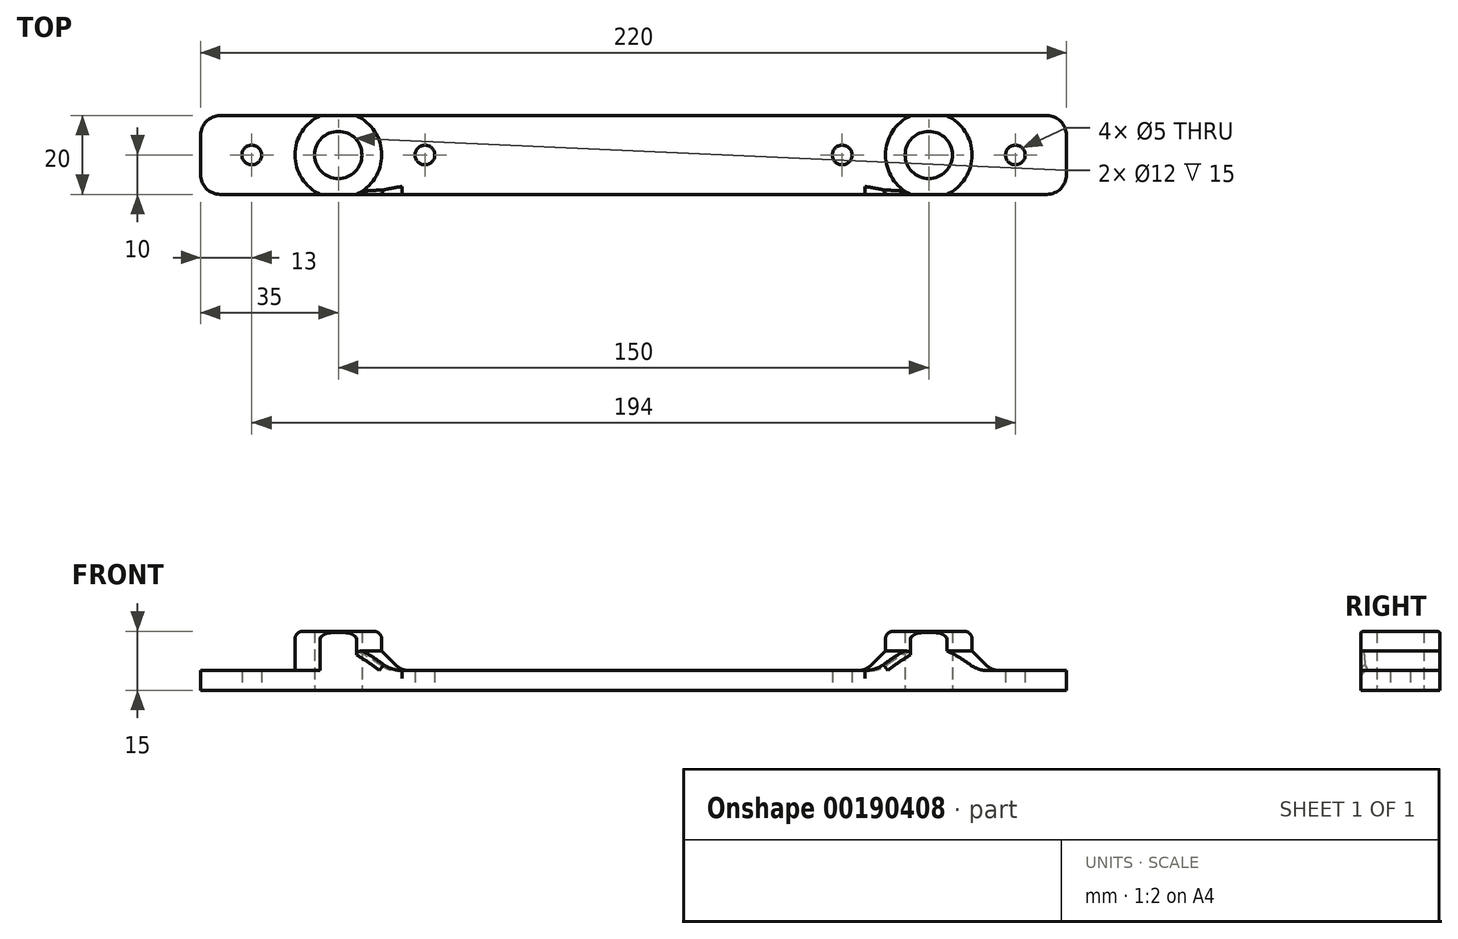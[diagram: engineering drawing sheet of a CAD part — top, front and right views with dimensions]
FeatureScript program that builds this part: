
annotation { "Feature Type Name" : "Feature", "Feature Type Description" : "" }
export const myFeature = defineFeature(function(context is Context, id is Id, definition is map)
    precondition{}
    {
        {
            var Q0;
            Q0=qCreatedBy(makeId("Top.planeOp"),FACE);
            var sketch = newSketch(context, id + "F0", { "sketchPlane" : qUnion([Q0])});
            skLineSegment(sketch, "E0.bottom", {"start": v(105, -10) * mm, "end": v(-105, -10) * mm});
            skLineSegment(sketch, "E0.top", {"start": v(105, 10) * mm, "end": v(-105, 10) * mm});
            skLineSegment(sketch, "E0.left", {"start": v(110, -5) * mm, "end": v(110, 5) * mm});
            skLineSegment(sketch, "E0.right", {"start": v(-110, -5) * mm, "end": v(-110, 5) * mm});
            skPoint(sketch, "E0.middle", {"position": v(0, 0) * mm});
            skCircle(sketch, "E1", {"center": v(-75, 0) * mm, "radius": 6 * mm});
            skCircle(sketch, "E2", {"center": v(75, 0) * mm, "radius": 6 * mm});
            skCircle(sketch, "E3", {"center": v(-53, 0) * mm, "radius": 2.5 * mm});
            skLineSegment(sketch, "E4", {"start": v(-75, 0) * mm, "end": v(-75, 26.01) * mm, "construction": true});
            skCircle(sketch, "E5.MirrorC", {"center": v(-97, 0) * mm, "radius": 2.5 * mm});
            skCircle(sketch, "E6.MirrorC", {"center": v(97, 0) * mm, "radius": 2.5 * mm});
            skCircle(sketch, "E7.MirrorC", {"center": v(53, 0) * mm, "radius": 2.5 * mm});
            skPoint(sketch, "E8.visualSharp", {"position": v(-110, 10) * mm});
            skArc(sketch, "E8.filletArc", {"start": v(-105, 10) * mm, "mid": v(-108.54, 8.54) * mm, "end": v(-110, 5) * mm});
            skPoint(sketch, "E9.visualSharp", {"position": v(-110, -10) * mm});
            skArc(sketch, "E9.filletArc", {"start": v(-110, -5) * mm, "mid": v(-108.54, -8.54) * mm, "end": v(-105, -10) * mm});
            skPoint(sketch, "E10.visualSharp", {"position": v(110, 10) * mm});
            skArc(sketch, "E10.filletArc", {"start": v(110, 5) * mm, "mid": v(108.54, 8.54) * mm, "end": v(105, 10) * mm});
            skPoint(sketch, "E11.visualSharp", {"position": v(110, -10) * mm});
            skArc(sketch, "E11.filletArc", {"start": v(105, -10) * mm, "mid": v(108.54, -8.54) * mm, "end": v(110, -5) * mm});
            skSolve(sketch);
        }
        {
            var Q0;
            Q0 = qSketchRegion(id + "F0", true);
            extrude(context, id + "F1", {"entities" : qUnion([Q0]), "depth" : 5 * mm});
        }
        {
            var Q0;
            Q0=makeQuery(id+"F1.opExtrude","CAP_FACE",FACE,{"disambiguationData":[OSD([sQuery(id+"F0.wireOp",EDGE,"E0.bottom"),sQuery(id+"F0.wireOp",EDGE,"E0.top"),sQuery(id+"F0.wireOp",EDGE,"E0.left"),sQuery(id+"F0.wireOp",EDGE,"E0.right"),sQuery(id+"F0.wireOp",EDGE,"E1"),sQuery(id+"F0.wireOp",EDGE,"E2"),sQuery(id+"F0.wireOp",EDGE,"E3"),sQuery(id+"F0.wireOp",EDGE,"E5.MirrorC"),sQuery(id+"F0.wireOp",EDGE,"E6.MirrorC"),sQuery(id+"F0.wireOp",EDGE,"E7.MirrorC")])],"isStart":false});
            var sketch = newSketch(context, id + "F2", { "sketchPlane" : qUnion([Q0])});
            skArc(sketch, "E12", {"start": v(-79.58, 10) * mm, "mid": v(-86, 0) * mm, "end": v(-79.58, -10) * mm});
            skLineSegment(sketch, "E13.0", {"start": v(-70.42, 10) * mm, "end": v(-79.58, 10) * mm});
            skLineSegment(sketch, "E14.0", {"start": v(-70.42, -10) * mm, "end": v(-79.58, -10) * mm});
            skPoint(sketch, "E15.orphan", {"position": v(105, 10) * mm});
            skPoint(sketch, "E16.orphan", {"position": v(105, -10) * mm});
            skArc(sketch, "E17.trimOffspring", {"start": v(-70.42, -10) * mm, "mid": v(-64, 0) * mm, "end": v(-70.42, 10) * mm});
            skArc(sketch, "E18.MirrorCS", {"start": v(70.42, -10) * mm, "mid": v(64, 0) * mm, "end": v(70.42, 10) * mm});
            skLineSegment(sketch, "E19.MirrorCS", {"start": v(70.42, -10) * mm, "end": v(79.58, -10) * mm});
            skLineSegment(sketch, "E20.MirrorCS", {"start": v(70.42, 10) * mm, "end": v(79.58, 10) * mm});
            skArc(sketch, "E21.MirrorCS", {"start": v(79.58, 10) * mm, "mid": v(86, 0) * mm, "end": v(79.58, -10) * mm});
            skCircle(sketch, "E22.0", {"center": v(-75, 0) * mm, "radius": 6 * mm});
            skCircle(sketch, "E23.0", {"center": v(75, 0) * mm, "radius": 6 * mm});
            skSolve(sketch);
        }
        {
            var Q0;
            Q0 = qSketchRegion(id + "F2", true);
            extrude(context, id + "F3", {"entities" : qUnion([Q0]), "operationType" : NewBodyOperationType.ADD, "depth" : 10 * mm});
        }
        {
            var Q0;
            Q0=makeQuery(id+"F3.opExtrude","CAP_EDGE",EDGE,{"disambiguationData":[OSD([sQuery(id+"F2.wireOp",EDGE,"E12")])],"isStart":true});
            var Q1;
            Q1=makeQuery(id+"F3.opExtrude","CAP_EDGE",EDGE,{"disambiguationData":[OSD([sQuery(id+"F2.wireOp",EDGE,"E17.trimOffspring")])],"isStart":true});
            var Q2;
            Q2=makeQuery(id+"F3.opExtrude","CAP_EDGE",EDGE,{"disambiguationData":[OSD([sQuery(id+"F2.wireOp",EDGE,"E18.MirrorCS")])],"isStart":true});
            var Q3;
            Q3=makeQuery(id+"F3.opExtrude","CAP_EDGE",EDGE,{"disambiguationData":[OSD([sQuery(id+"F2.wireOp",EDGE,"E21.MirrorCS")])],"isStart":true});
            chamfer(context, id + "F4", {"entities" : qUnion([Q0, Q1, Q2, Q3]), "width" : 5 * mm, "tangentPropagation" : true});
        }
        {
            var Q0;
            {var subQ0=sQuery(id+"F0.wireOp",EDGE,"E9.filletArc");var subQ1=sQuery(id+"F0.wireOp",EDGE,"E0.bottom");var subQ2=sQuery(id+"F2.wireOp",EDGE,"E12");var subQ3=sQuery(id+"F0.wireOp",EDGE,"E0.top");var subQ4=sQuery(id+"F0.wireOp",EDGE,"E5.MirrorC");var subQ5=sQuery(id+"F0.wireOp",EDGE,"E8.filletArc");var subQ6=sQuery(id+"F0.wireOp",EDGE,"E0.right");Q0=makeQuery(id+"F4.opChamfer","BLEND_EDGE",EDGE,{"blendedFrom":[makeQuery(id+"F3.opExtrude","CAP_EDGE",EDGE,{"disambiguationData":[OSD([subQ2])],"isStart":true}),makeQuery(id+"F3.boolean.opBoolean","SPLIT",FACE,{"disambiguationData":[TD([makeQuery(id+"F1.opExtrude","SWEPT_FACE",FACE,{"disambiguationData":[OSD([subQ6])]})])],"derivedFrom":makeQuery(id+"F1.opExtrude","CAP_FACE",FACE,{"disambiguationData":[OSD([subQ1,subQ3,sQuery(id+"F0.wireOp",EDGE,"E0.left"),subQ6,sQuery(id+"F0.wireOp",EDGE,"E1"),sQuery(id+"F0.wireOp",EDGE,"E2"),sQuery(id+"F0.wireOp",EDGE,"E3"),subQ4,sQuery(id+"F0.wireOp",EDGE,"E6.MirrorC"),sQuery(id+"F0.wireOp",EDGE,"E7.MirrorC"),subQ5,subQ0,sQuery(id+"F0.wireOp",EDGE,"E10.filletArc"),sQuery(id+"F0.wireOp",EDGE,"E11.filletArc")])],"isStart":false})})],"blendedInto":[makeQuery(id+"F3.boolean.opBoolean","SPLIT",FACE,{"disambiguationData":[TD([makeQuery(id+"F1.opExtrude","SWEPT_FACE",FACE,{"disambiguationData":[OSD([subQ6])]})])],"derivedFrom":makeQuery(id+"F1.opExtrude","CAP_FACE",FACE,{"disambiguationData":[OSD([subQ1,subQ3,sQuery(id+"F0.wireOp",EDGE,"E0.left"),subQ6,sQuery(id+"F0.wireOp",EDGE,"E1"),sQuery(id+"F0.wireOp",EDGE,"E2"),sQuery(id+"F0.wireOp",EDGE,"E3"),subQ4,sQuery(id+"F0.wireOp",EDGE,"E6.MirrorC"),sQuery(id+"F0.wireOp",EDGE,"E7.MirrorC"),subQ5,subQ0,sQuery(id+"F0.wireOp",EDGE,"E10.filletArc"),sQuery(id+"F0.wireOp",EDGE,"E11.filletArc")])],"isStart":false})})]});}
            var Q1;
            {var subQ0=sQuery(id+"F2.wireOp",EDGE,"E12");Q1=makeQuery(id+"F4.opChamfer","BLEND_EDGE",EDGE,{"blendedFrom":[makeQuery(id+"F3.opExtrude","CAP_EDGE",EDGE,{"disambiguationData":[OSD([subQ0])],"isStart":true}),makeQuery(id+"F3.opExtrude","CAP_FACE",FACE,{"disambiguationData":[OSD([subQ0,sQuery(id+"F2.wireOp",EDGE,"E13.0"),sQuery(id+"F2.wireOp",EDGE,"E14.0"),sQuery(id+"F2.wireOp",EDGE,"E17.trimOffspring"),sQuery(id+"F2.wireOp",EDGE,"E22.0")])],"isStart":false})],"blendedInto":[makeQuery(id+"F3.opExtrude","CAP_FACE",FACE,{"disambiguationData":[OSD([subQ0,sQuery(id+"F2.wireOp",EDGE,"E13.0"),sQuery(id+"F2.wireOp",EDGE,"E14.0"),sQuery(id+"F2.wireOp",EDGE,"E17.trimOffspring"),sQuery(id+"F2.wireOp",EDGE,"E22.0")])],"isStart":false})]});}
            var Q2;
            {var subQ0=sQuery(id+"F0.wireOp",EDGE,"E7.MirrorC");var subQ1=sQuery(id+"F0.wireOp",EDGE,"E3");var subQ2=sQuery(id+"F2.wireOp",EDGE,"E17.trimOffspring");var subQ3=sQuery(id+"F0.wireOp",EDGE,"E0.top");var subQ4=sQuery(id+"F0.wireOp",EDGE,"E0.bottom");Q2=makeQuery(id+"F4.opChamfer","BLEND_EDGE",EDGE,{"blendedFrom":[makeQuery(id+"F3.opExtrude","CAP_EDGE",EDGE,{"disambiguationData":[OSD([subQ2])],"isStart":true}),makeQuery(id+"F3.boolean.opBoolean","SPLIT",FACE,{"disambiguationData":[TD([makeQuery(id+"F1.opExtrude","SWEPT_FACE",FACE,{"disambiguationData":[OSD([subQ1])]})])],"derivedFrom":makeQuery(id+"F1.opExtrude","CAP_FACE",FACE,{"disambiguationData":[OSD([subQ4,subQ3,sQuery(id+"F0.wireOp",EDGE,"E0.left"),sQuery(id+"F0.wireOp",EDGE,"E0.right"),sQuery(id+"F0.wireOp",EDGE,"E1"),sQuery(id+"F0.wireOp",EDGE,"E2"),subQ1,sQuery(id+"F0.wireOp",EDGE,"E5.MirrorC"),sQuery(id+"F0.wireOp",EDGE,"E6.MirrorC"),subQ0,sQuery(id+"F0.wireOp",EDGE,"E8.filletArc"),sQuery(id+"F0.wireOp",EDGE,"E9.filletArc"),sQuery(id+"F0.wireOp",EDGE,"E10.filletArc"),sQuery(id+"F0.wireOp",EDGE,"E11.filletArc")])],"isStart":false})})],"blendedInto":[makeQuery(id+"F3.boolean.opBoolean","SPLIT",FACE,{"disambiguationData":[TD([makeQuery(id+"F1.opExtrude","SWEPT_FACE",FACE,{"disambiguationData":[OSD([subQ1])]})])],"derivedFrom":makeQuery(id+"F1.opExtrude","CAP_FACE",FACE,{"disambiguationData":[OSD([subQ4,subQ3,sQuery(id+"F0.wireOp",EDGE,"E0.left"),sQuery(id+"F0.wireOp",EDGE,"E0.right"),sQuery(id+"F0.wireOp",EDGE,"E1"),sQuery(id+"F0.wireOp",EDGE,"E2"),subQ1,sQuery(id+"F0.wireOp",EDGE,"E5.MirrorC"),sQuery(id+"F0.wireOp",EDGE,"E6.MirrorC"),subQ0,sQuery(id+"F0.wireOp",EDGE,"E8.filletArc"),sQuery(id+"F0.wireOp",EDGE,"E9.filletArc"),sQuery(id+"F0.wireOp",EDGE,"E10.filletArc"),sQuery(id+"F0.wireOp",EDGE,"E11.filletArc")])],"isStart":false})})]});}
            var Q3;
            {var subQ0=sQuery(id+"F0.wireOp",EDGE,"E7.MirrorC");var subQ1=sQuery(id+"F0.wireOp",EDGE,"E3");var subQ2=sQuery(id+"F0.wireOp",EDGE,"E0.top");var subQ3=sQuery(id+"F0.wireOp",EDGE,"E0.bottom");var subQ4=sQuery(id+"F2.wireOp",EDGE,"E18.MirrorCS");Q3=makeQuery(id+"F4.opChamfer","BLEND_EDGE",EDGE,{"blendedFrom":[makeQuery(id+"F3.opExtrude","CAP_EDGE",EDGE,{"disambiguationData":[OSD([subQ4])],"isStart":true}),makeQuery(id+"F3.boolean.opBoolean","SPLIT",FACE,{"disambiguationData":[TD([makeQuery(id+"F1.opExtrude","SWEPT_FACE",FACE,{"disambiguationData":[OSD([subQ1])]})])],"derivedFrom":makeQuery(id+"F1.opExtrude","CAP_FACE",FACE,{"disambiguationData":[OSD([subQ3,subQ2,sQuery(id+"F0.wireOp",EDGE,"E0.left"),sQuery(id+"F0.wireOp",EDGE,"E0.right"),sQuery(id+"F0.wireOp",EDGE,"E1"),sQuery(id+"F0.wireOp",EDGE,"E2"),subQ1,sQuery(id+"F0.wireOp",EDGE,"E5.MirrorC"),sQuery(id+"F0.wireOp",EDGE,"E6.MirrorC"),subQ0,sQuery(id+"F0.wireOp",EDGE,"E8.filletArc"),sQuery(id+"F0.wireOp",EDGE,"E9.filletArc"),sQuery(id+"F0.wireOp",EDGE,"E10.filletArc"),sQuery(id+"F0.wireOp",EDGE,"E11.filletArc")])],"isStart":false})})],"blendedInto":[makeQuery(id+"F3.boolean.opBoolean","SPLIT",FACE,{"disambiguationData":[TD([makeQuery(id+"F1.opExtrude","SWEPT_FACE",FACE,{"disambiguationData":[OSD([subQ1])]})])],"derivedFrom":makeQuery(id+"F1.opExtrude","CAP_FACE",FACE,{"disambiguationData":[OSD([subQ3,subQ2,sQuery(id+"F0.wireOp",EDGE,"E0.left"),sQuery(id+"F0.wireOp",EDGE,"E0.right"),sQuery(id+"F0.wireOp",EDGE,"E1"),sQuery(id+"F0.wireOp",EDGE,"E2"),subQ1,sQuery(id+"F0.wireOp",EDGE,"E5.MirrorC"),sQuery(id+"F0.wireOp",EDGE,"E6.MirrorC"),subQ0,sQuery(id+"F0.wireOp",EDGE,"E8.filletArc"),sQuery(id+"F0.wireOp",EDGE,"E9.filletArc"),sQuery(id+"F0.wireOp",EDGE,"E10.filletArc"),sQuery(id+"F0.wireOp",EDGE,"E11.filletArc")])],"isStart":false})})]});}
            var Q4;
            {var subQ0=sQuery(id+"F2.wireOp",EDGE,"E18.MirrorCS");Q4=makeQuery(id+"F4.opChamfer","BLEND_EDGE",EDGE,{"blendedFrom":[makeQuery(id+"F3.opExtrude","CAP_EDGE",EDGE,{"disambiguationData":[OSD([subQ0])],"isStart":true}),makeQuery(id+"F3.opExtrude","CAP_FACE",FACE,{"disambiguationData":[OSD([subQ0,sQuery(id+"F2.wireOp",EDGE,"E19.MirrorCS"),sQuery(id+"F2.wireOp",EDGE,"E20.MirrorCS"),sQuery(id+"F2.wireOp",EDGE,"E21.MirrorCS"),sQuery(id+"F2.wireOp",EDGE,"E23.0")])],"isStart":false})],"blendedInto":[makeQuery(id+"F3.opExtrude","CAP_FACE",FACE,{"disambiguationData":[OSD([subQ0,sQuery(id+"F2.wireOp",EDGE,"E19.MirrorCS"),sQuery(id+"F2.wireOp",EDGE,"E20.MirrorCS"),sQuery(id+"F2.wireOp",EDGE,"E21.MirrorCS"),sQuery(id+"F2.wireOp",EDGE,"E23.0")])],"isStart":false})]});}
            var Q5;
            {var subQ0=sQuery(id+"F2.wireOp",EDGE,"E21.MirrorCS");Q5=makeQuery(id+"F4.opChamfer","BLEND_EDGE",EDGE,{"blendedFrom":[makeQuery(id+"F3.opExtrude","CAP_EDGE",EDGE,{"disambiguationData":[OSD([subQ0])],"isStart":true}),makeQuery(id+"F3.opExtrude","CAP_FACE",FACE,{"disambiguationData":[OSD([sQuery(id+"F2.wireOp",EDGE,"E18.MirrorCS"),sQuery(id+"F2.wireOp",EDGE,"E19.MirrorCS"),sQuery(id+"F2.wireOp",EDGE,"E20.MirrorCS"),subQ0,sQuery(id+"F2.wireOp",EDGE,"E23.0")])],"isStart":false})],"blendedInto":[makeQuery(id+"F3.opExtrude","CAP_FACE",FACE,{"disambiguationData":[OSD([sQuery(id+"F2.wireOp",EDGE,"E18.MirrorCS"),sQuery(id+"F2.wireOp",EDGE,"E19.MirrorCS"),sQuery(id+"F2.wireOp",EDGE,"E20.MirrorCS"),subQ0,sQuery(id+"F2.wireOp",EDGE,"E23.0")])],"isStart":false})]});}
            var Q6;
            {var subQ0=sQuery(id+"F0.wireOp",EDGE,"E0.left");var subQ1=sQuery(id+"F0.wireOp",EDGE,"E11.filletArc");var subQ2=sQuery(id+"F0.wireOp",EDGE,"E10.filletArc");var subQ3=sQuery(id+"F0.wireOp",EDGE,"E0.bottom");var subQ4=sQuery(id+"F0.wireOp",EDGE,"E0.top");var subQ5=sQuery(id+"F0.wireOp",EDGE,"E6.MirrorC");var subQ6=sQuery(id+"F2.wireOp",EDGE,"E21.MirrorCS");Q6=makeQuery(id+"F4.opChamfer","BLEND_EDGE",EDGE,{"blendedFrom":[makeQuery(id+"F3.opExtrude","CAP_EDGE",EDGE,{"disambiguationData":[OSD([subQ6])],"isStart":true}),makeQuery(id+"F3.boolean.opBoolean","SPLIT",FACE,{"disambiguationData":[TD([makeQuery(id+"F1.opExtrude","SWEPT_FACE",FACE,{"disambiguationData":[OSD([subQ0])]})])],"derivedFrom":makeQuery(id+"F1.opExtrude","CAP_FACE",FACE,{"disambiguationData":[OSD([subQ3,subQ4,subQ0,sQuery(id+"F0.wireOp",EDGE,"E0.right"),sQuery(id+"F0.wireOp",EDGE,"E1"),sQuery(id+"F0.wireOp",EDGE,"E2"),sQuery(id+"F0.wireOp",EDGE,"E3"),sQuery(id+"F0.wireOp",EDGE,"E5.MirrorC"),subQ5,sQuery(id+"F0.wireOp",EDGE,"E7.MirrorC"),sQuery(id+"F0.wireOp",EDGE,"E8.filletArc"),sQuery(id+"F0.wireOp",EDGE,"E9.filletArc"),subQ2,subQ1])],"isStart":false})})],"blendedInto":[makeQuery(id+"F3.boolean.opBoolean","SPLIT",FACE,{"disambiguationData":[TD([makeQuery(id+"F1.opExtrude","SWEPT_FACE",FACE,{"disambiguationData":[OSD([subQ0])]})])],"derivedFrom":makeQuery(id+"F1.opExtrude","CAP_FACE",FACE,{"disambiguationData":[OSD([subQ3,subQ4,subQ0,sQuery(id+"F0.wireOp",EDGE,"E0.right"),sQuery(id+"F0.wireOp",EDGE,"E1"),sQuery(id+"F0.wireOp",EDGE,"E2"),sQuery(id+"F0.wireOp",EDGE,"E3"),sQuery(id+"F0.wireOp",EDGE,"E5.MirrorC"),subQ5,sQuery(id+"F0.wireOp",EDGE,"E7.MirrorC"),sQuery(id+"F0.wireOp",EDGE,"E8.filletArc"),sQuery(id+"F0.wireOp",EDGE,"E9.filletArc"),subQ2,subQ1])],"isStart":false})})]});}
            fillet(context, id + "F5", {"entities" : qUnion([Q0, Q1, Q2, Q3, Q4, Q5, Q6]), "radius" : 5 * mm, "tangentPropagation" : true, "allowEdgeOverflow" : false});
        }
        {
            var Q0;
            {var subQ0=sQuery(id+"F0.wireOp",EDGE,"E0.bottom");Q0=makeQuery(id+"F3.boolean.opBoolean","SPLIT",EDGE,{"disambiguationData":[TD([makeQuery(id+"F3.opExtrude","SWEPT_FACE",FACE,{"disambiguationData":[OSD([sQuery(id+"F2.wireOp",EDGE,"E17.trimOffspring")])]})])],"derivedFrom":makeQuery(id+"F1.opExtrude","CAP_EDGE",EDGE,{"disambiguationData":[OSD([subQ0])],"isStart":false})});}
            fillet(context, id + "F6", {"entities" : qUnion([Q0]), "radius" : 2 * mm, "tangentPropagation" : true, "allowEdgeOverflow" : false});
        }
        {
            var Q0;
            Q0=makeQuery(id+"F3.opExtrude","CAP_EDGE",EDGE,{"disambiguationData":[OSD([sQuery(id+"F2.wireOp",EDGE,"E17.trimOffspring")])],"isStart":false});
            var Q1;
            Q1=makeQuery(id+"F3.opExtrude","CAP_EDGE",EDGE,{"disambiguationData":[OSD([sQuery(id+"F2.wireOp",EDGE,"E21.MirrorCS")])],"isStart":false});
            fillet(context, id + "F7", {"entities" : qUnion([Q0, Q1]), "radius" : 2 * mm, "tangentPropagation" : true, "allowEdgeOverflow" : false});
        }
    });
